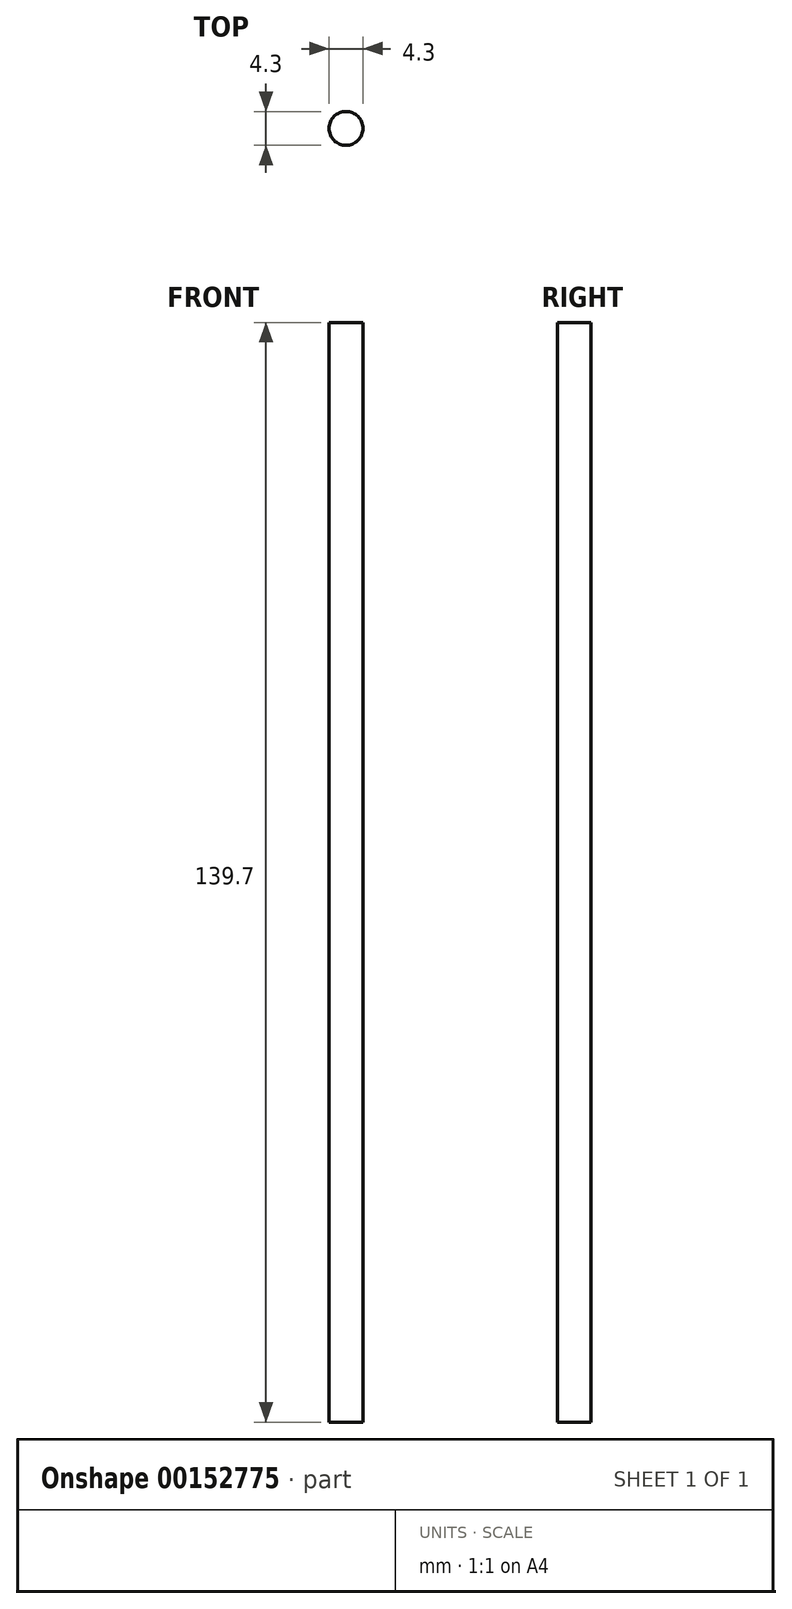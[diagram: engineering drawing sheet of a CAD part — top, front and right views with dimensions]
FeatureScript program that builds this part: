
annotation { "Feature Type Name" : "Feature", "Feature Type Description" : "" }
export const myFeature = defineFeature(function(context is Context, id is Id, definition is map)
    precondition{}
    {
        {
            var Q0;
            Q0=qCreatedBy(makeId("Top.planeOp"),FACE);
            var sketch = newSketch(context, id + "F0", { "sketchPlane" : qUnion([Q0])});
            skCircle(sketch, "E0", {"center": v(0, 0) * mm, "radius": 2.15 * mm});
            skSolve(sketch);
        }
        {
            var Q0;
            Q0=qSketchRegion(id+"F0",true);
            extrude(context, id + "F1", {"entities" : qUnion([Q0]), "depth" : 139.7 * mm});
        }
    });
